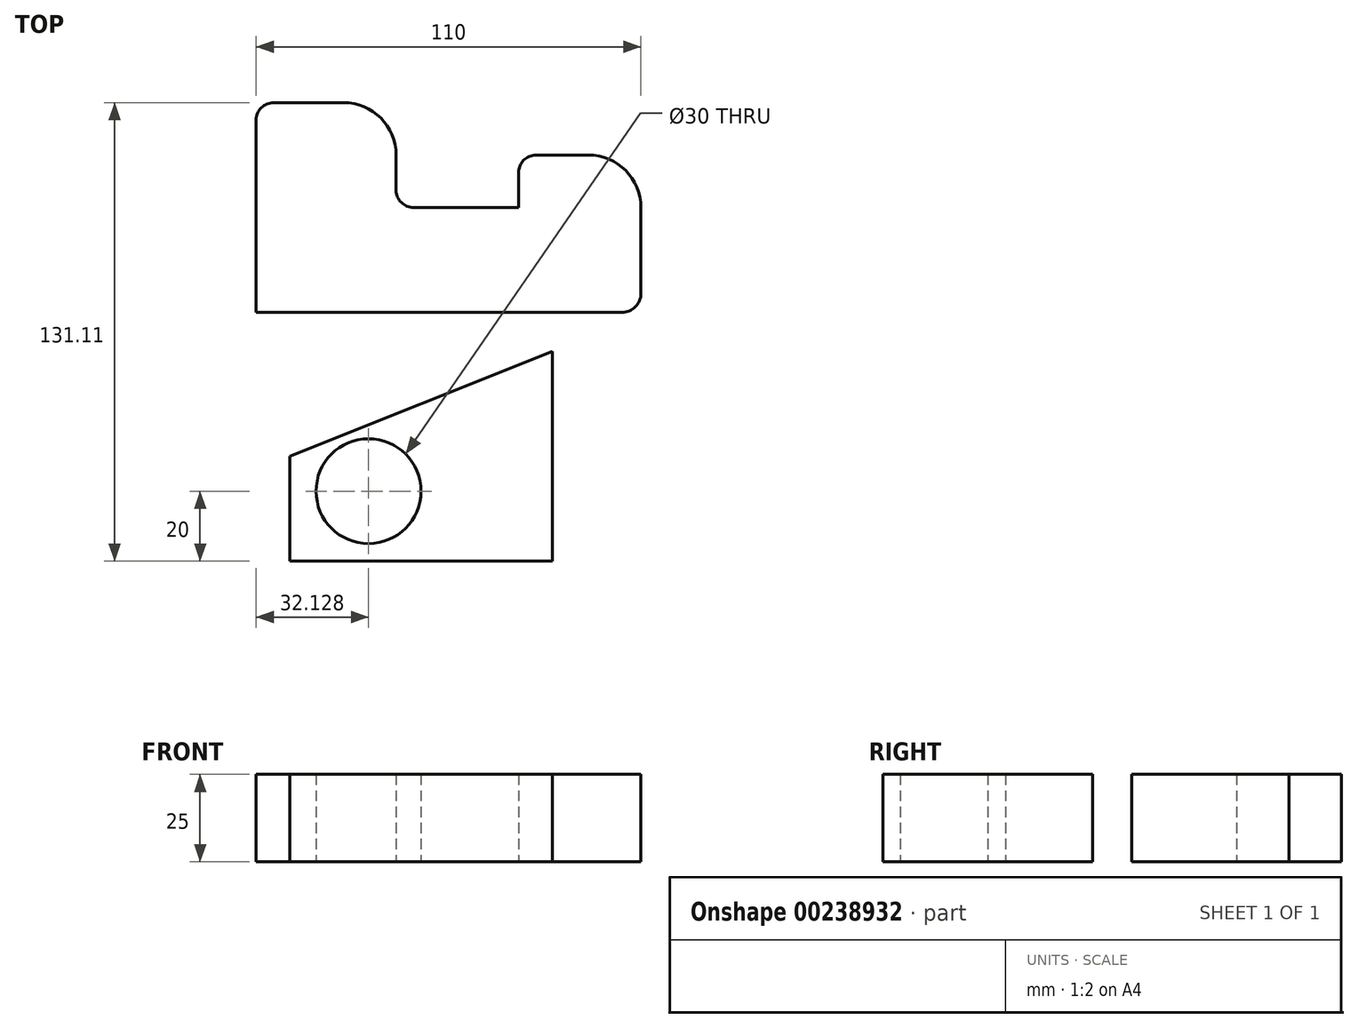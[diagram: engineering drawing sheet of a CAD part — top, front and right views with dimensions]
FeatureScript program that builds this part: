
annotation { "Feature Type Name" : "Feature", "Feature Type Description" : "" }
export const myFeature = defineFeature(function(context is Context, id is Id, definition is map)
    precondition{}
    {
        {
            var Q0;
            Q0=qCreatedBy(makeId("Top.planeOp"),FACE);
            var sketch = newSketch(context, id + "F0", { "sketchPlane" : qUnion([Q0])});
            skLineSegment(sketch, "E0", {"start": v(-52.66, 2.39) * mm, "end": v(51.84, 2.39) * mm});
            skLineSegment(sketch, "E1", {"start": v(57.34, 7.89) * mm, "end": v(57.34, 32.39) * mm});
            skLineSegment(sketch, "E2", {"start": v(42.34, 47.39) * mm, "end": v(27.34, 47.39) * mm});
            skLineSegment(sketch, "E3", {"start": v(22.34, 42.39) * mm, "end": v(22.34, 32.39) * mm});
            skLineSegment(sketch, "E4", {"start": v(22.34, 32.39) * mm, "end": v(-7.66, 32.39) * mm});
            skLineSegment(sketch, "E5", {"start": v(-12.66, 37.39) * mm, "end": v(-12.66, 47.39) * mm});
            skLineSegment(sketch, "E6", {"start": v(-27.66, 62.39) * mm, "end": v(-47.66, 62.39) * mm});
            skLineSegment(sketch, "E7", {"start": v(-52.66, 57.39) * mm, "end": v(-52.66, 2.39) * mm});
            skPoint(sketch, "E8.visualSharp", {"position": v(-52.66, 62.39) * mm});
            skArc(sketch, "E8.filletArc", {"start": v(-47.66, 62.39) * mm, "mid": v(-51.2, 60.93) * mm, "end": v(-52.66, 57.39) * mm});
            skPoint(sketch, "E9.visualSharp", {"position": v(-12.66, 62.39) * mm});
            skArc(sketch, "E9.filletArc", {"start": v(-12.66, 47.39) * mm, "mid": v(-17.05, 58) * mm, "end": v(-27.66, 62.39) * mm});
            skPoint(sketch, "E10.visualSharp", {"position": v(-12.66, 32.39) * mm});
            skArc(sketch, "E10.filletArc", {"start": v(-12.66, 37.39) * mm, "mid": v(-11.2, 33.85) * mm, "end": v(-7.66, 32.39) * mm});
            skPoint(sketch, "E11.visualSharp", {"position": v(22.34, 47.39) * mm});
            skArc(sketch, "E11.filletArc", {"start": v(27.34, 47.39) * mm, "mid": v(23.8, 45.93) * mm, "end": v(22.34, 42.39) * mm});
            skPoint(sketch, "E12.visualSharp", {"position": v(57.34, 47.39) * mm});
            skArc(sketch, "E12.filletArc", {"start": v(57.34, 32.39) * mm, "mid": v(52.95, 43) * mm, "end": v(42.34, 47.39) * mm});
            skPoint(sketch, "E13.visualSharp", {"position": v(57.34, 2.39) * mm});
            skArc(sketch, "E13.filletArc", {"start": v(51.84, 2.39) * mm, "mid": v(55.73, 4) * mm, "end": v(57.34, 7.89) * mm});
            skLineSegment(sketch, "E14", {"start": v(-43.03, -68.72) * mm, "end": v(-43.03, -38.72) * mm});
            skLineSegment(sketch, "E15", {"start": v(-43.03, -38.72) * mm, "end": v(31.97, -8.72) * mm});
            skLineSegment(sketch, "E16", {"start": v(31.97, -8.72) * mm, "end": v(31.97, -68.72) * mm});
            skLineSegment(sketch, "E17", {"start": v(31.97, -68.72) * mm, "end": v(-43.03, -68.72) * mm});
            skCircle(sketch, "E18", {"center": v(-20.53, -48.72) * mm, "radius": 15 * mm});
            skSolve(sketch);
        }
        {
            var Q0;
            Q0 = qSketchRegion(id + "F0", true);
            extrude(context, id + "F1", {"entities" : qUnion([Q0]), "depth" : 25 * mm});
        }
    });
